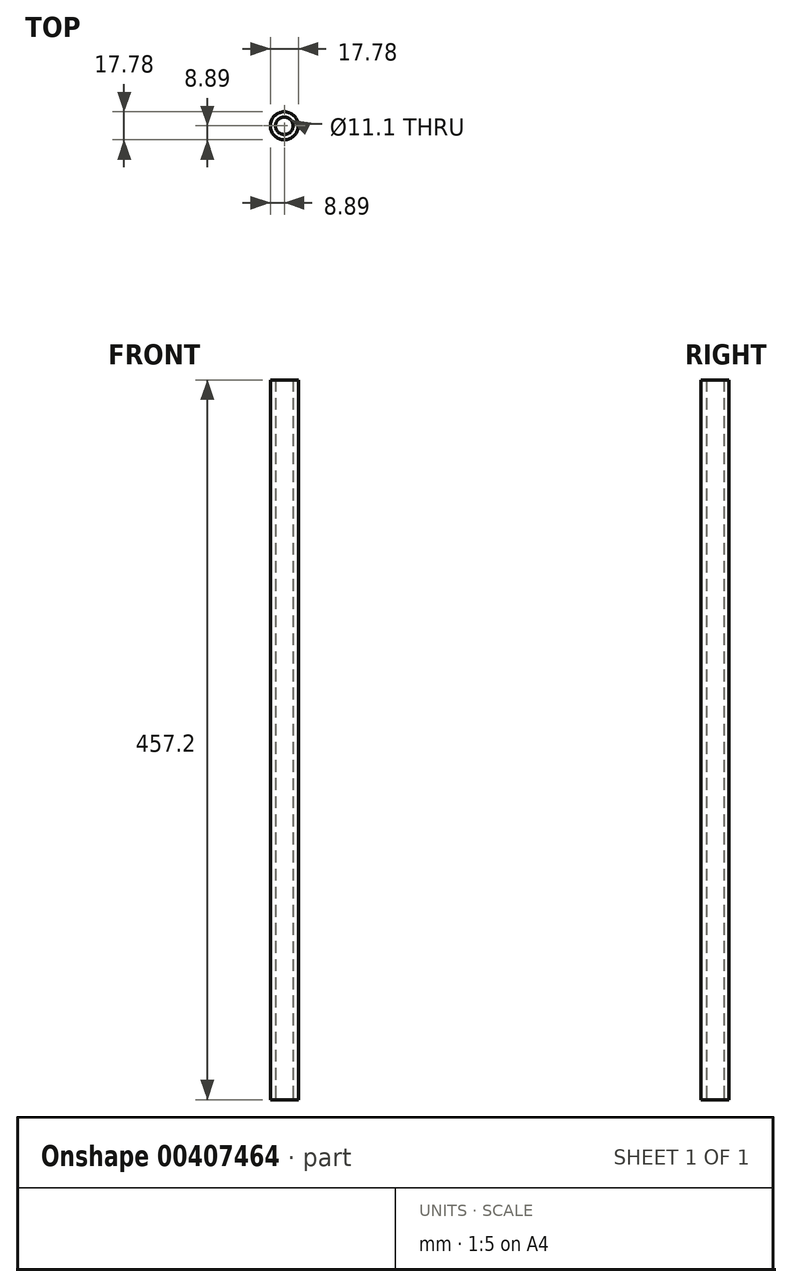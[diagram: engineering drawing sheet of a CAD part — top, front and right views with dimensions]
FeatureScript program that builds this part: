
annotation { "Feature Type Name" : "Feature", "Feature Type Description" : "" }
export const myFeature = defineFeature(function(context is Context, id is Id, definition is map)
    precondition{}
    {
        {
            var Q0;
            Q0=qCreatedBy(makeId("Top.planeOp"),FACE);
            var sketch = newSketch(context, id + "F0", { "sketchPlane" : qUnion([Q0])});
            skCircle(sketch, "E0", {"center": v(0, 0) * mm, "radius": 5.55 * mm});
            skCircle(sketch, "E1", {"center": v(0, 0) * mm, "radius": 8.9 * mm});
            skSolve(sketch);
        }
        {
            var Q0;
            Q0=makeQuery(id+"F0.imprint","IMPRINT",FACE,{"disambiguationData":[TD([[makeQuery(id+"F0.imprint","IMPRINT",EDGE,{"derivedFrom":sQuery(id+"F0.wireOp",EDGE,"E0")}),-1.0]])]});
            extrude(context, id + "F1", {"entities" : qUnion([Q0]), "depth" : 254 * mm, "hasSecondDirection" : true, "secondDirectionOppositeDirection" : true, "secondDirectionDepth" : 203.2 * mm});
        }
    });
